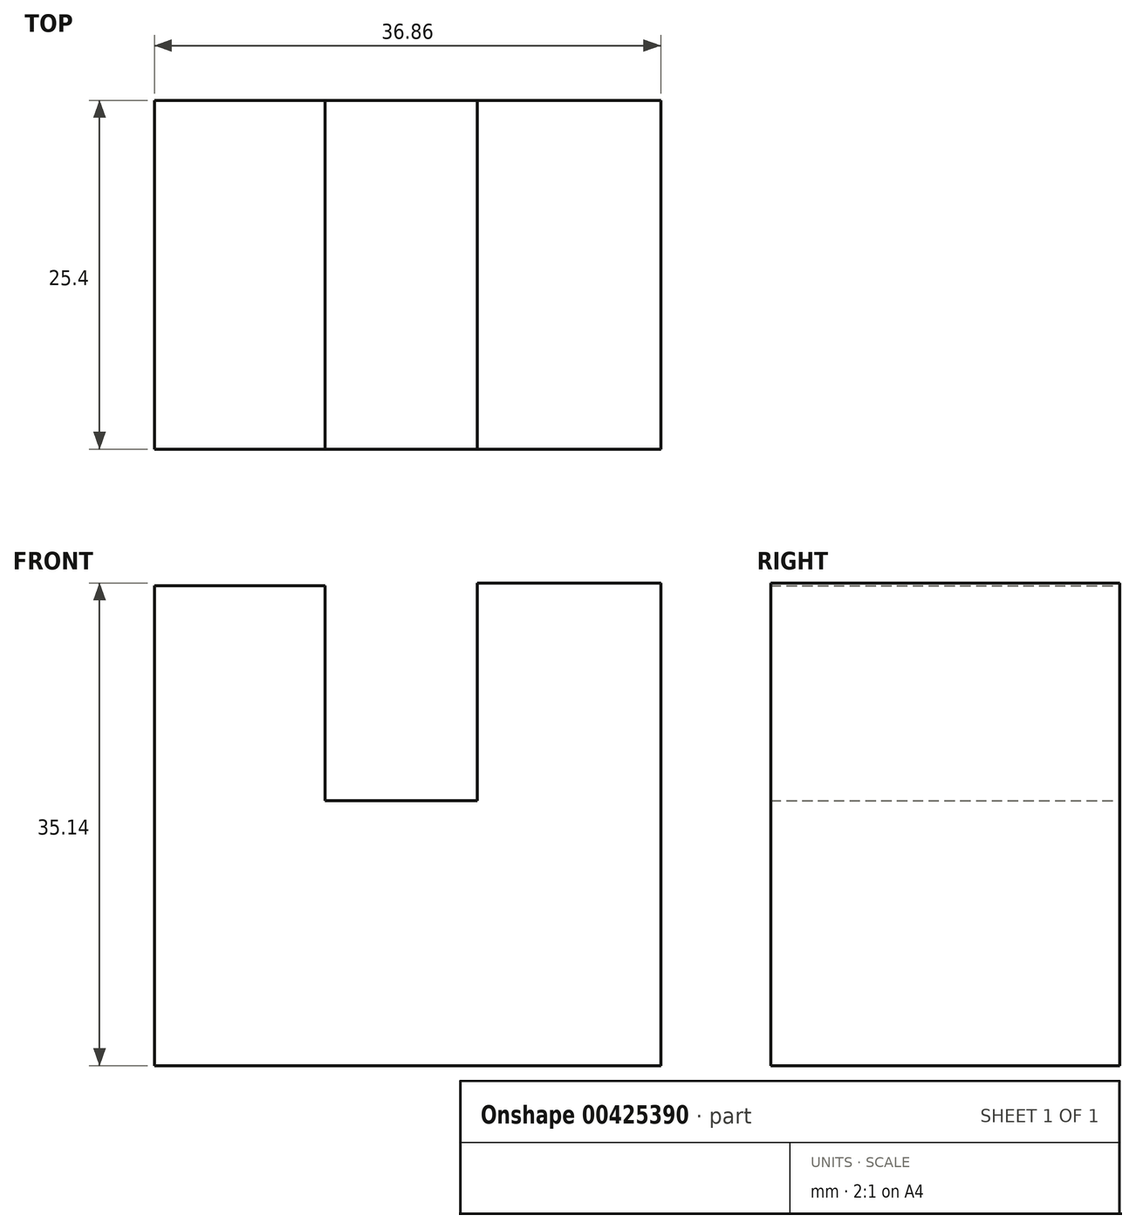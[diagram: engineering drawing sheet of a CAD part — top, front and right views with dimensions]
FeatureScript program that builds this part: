
annotation { "Feature Type Name" : "Feature", "Feature Type Description" : "" }
export const myFeature = defineFeature(function(context is Context, id is Id, definition is map)
    precondition{}
    {
        {
            var Q0;
            Q0=qCreatedBy(makeId("Front.planeOp"),FACE);
            var sketch = newSketch(context, id + "F0", { "sketchPlane" : qUnion([Q0])});
            skLineSegment(sketch, "E0", {"start": v(-63.59, 56.52) * mm, "end": v(-63.59, 0) * mm});
            skLineSegment(sketch, "E1", {"start": v(-63.59, 0) * mm, "end": v(-8.4, 0) * mm});
            skLineSegment(sketch, "E2", {"start": v(-8.4, 0) * mm, "end": v(-8.4, 56.52) * mm});
            skLineSegment(sketch, "E3", {"start": v(-8.4, 56.52) * mm, "end": v(-21.96, 56.52) * mm});
            skLineSegment(sketch, "E4", {"start": v(-21.96, 56.52) * mm, "end": v(-21.96, 11.65) * mm});
            skLineSegment(sketch, "E5", {"start": v(-21.96, 11.65) * mm, "end": v(-51.18, 11.65) * mm});
            skLineSegment(sketch, "E6", {"start": v(-51.18, 11.65) * mm, "end": v(-51.18, 56.71) * mm});
            skLineSegment(sketch, "E7", {"start": v(-51.18, 56.71) * mm, "end": v(-63.59, 56.52) * mm});
            skSolve(sketch);
        }
        {
            var Q0;
            Q0=makeQuery(id+"F0.imprint","IMPRINT",FACE,{"disambiguationData":[TD([[makeQuery(id+"F0.imprint","IMPRINT",EDGE,{"derivedFrom":sQuery(id+"F0.wireOp",EDGE,"E0")}),1.0]])]});
            extrude(context, id + "F1", {"entities" : qUnion([Q0]), "depth" : 25.4 * mm});
        }
        {
            var Q0;
            Q0=makeQuery(id+"F1.opExtrude","SWEPT_BODY",BODY,{"disambiguationData":[OSD([sQuery(id+"F0.wireOp",EDGE,"E0"),sQuery(id+"F0.wireOp",EDGE,"E1"),sQuery(id+"F0.wireOp",EDGE,"E2"),sQuery(id+"F0.wireOp",EDGE,"E3"),sQuery(id+"F0.wireOp",EDGE,"E4"),sQuery(id+"F0.wireOp",EDGE,"E5"),sQuery(id+"F0.wireOp",EDGE,"E6"),sQuery(id+"F0.wireOp",EDGE,"E7")])]});
            deleteBodies(context, id + "F2", {"entities" : qUnion([Q0])});
        }
        {
            var Q0;
            Q0=qCreatedBy(makeId("Front.planeOp"),FACE);
            var sketch = newSketch(context, id + "F3", { "sketchPlane" : qUnion([Q0])});
            skLineSegment(sketch, "E8", {"start": v(-61.3, 33.42) * mm, "end": v(-61.3, 0) * mm});
            skLineSegment(sketch, "E9", {"start": v(-61.3, 0) * mm, "end": v(-24.44, 0) * mm});
            skLineSegment(sketch, "E10", {"start": v(-24.44, 0) * mm, "end": v(-24.44, 35.14) * mm});
            skLineSegment(sketch, "E11", {"start": v(-24.44, 35.14) * mm, "end": v(-37.8, 35.14) * mm});
            skLineSegment(sketch, "E12", {"start": v(-37.8, 35.14) * mm, "end": v(-37.8, 19.29) * mm});
            skLineSegment(sketch, "E13", {"start": v(-37.8, 19.29) * mm, "end": v(-48.88, 19.29) * mm});
            skLineSegment(sketch, "E14", {"start": v(-48.88, 19.29) * mm, "end": v(-48.88, 34.94) * mm});
            skLineSegment(sketch, "E15", {"start": v(-48.88, 34.94) * mm, "end": v(-61.3, 34.94) * mm});
            skLineSegment(sketch, "E16", {"start": v(-61.3, 34.94) * mm, "end": v(-61.3, 33.42) * mm});
            skSolve(sketch);
        }
        {
            var Q0;
            Q0=makeQuery(id+"F3.imprint","IMPRINT",FACE,{"disambiguationData":[TD([[makeQuery(id+"F3.imprint","IMPRINT",EDGE,{"derivedFrom":sQuery(id+"F3.wireOp",EDGE,"E8")}),1.0]])]});
            extrude(context, id + "F4", {"entities" : qUnion([Q0]), "depth" : 25.4 * mm});
        }
    });
